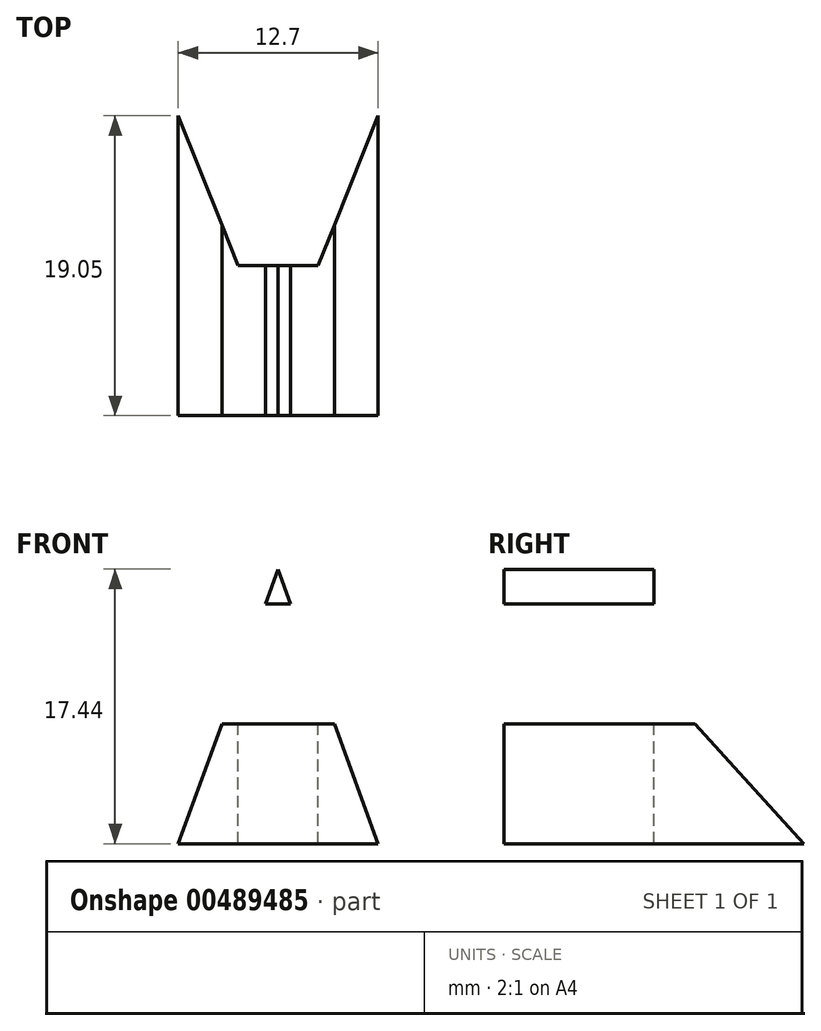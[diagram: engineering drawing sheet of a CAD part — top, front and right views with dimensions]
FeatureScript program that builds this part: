
annotation { "Feature Type Name" : "Feature", "Feature Type Description" : "" }
export const myFeature = defineFeature(function(context is Context, id is Id, definition is map)
    precondition{}
    {
        {
            var Q0;
            Q0=qCreatedBy(makeId("Front.planeOp"),FACE);
            var sketch = newSketch(context, id + "F0", { "sketchPlane" : qUnion([Q0])});
            skLineSegment(sketch, "E0", {"start": v(0, 0) * mm, "end": v(38.1, 0) * mm});
            skLineSegment(sketch, "E1", {"start": v(38.1, 0) * mm, "end": v(38.1, 38.1) * mm});
            skLineSegment(sketch, "E2", {"start": v(38.1, 38.1) * mm, "end": v(0, 38.1) * mm});
            skLineSegment(sketch, "E3", {"start": v(0, 38.1) * mm, "end": v(0, 0) * mm});
            skSolve(sketch);
        }
        {
            var Q0;
            Q0=makeQuery(id+"F0.imprint","IMPRINT",FACE,{"disambiguationData":[TD([[makeQuery(id+"F0.imprint","IMPRINT",EDGE,{"derivedFrom":sQuery(id+"F0.wireOp",EDGE,"E0")}),1.0]])]});
            extrude(context, id + "F1", {"entities" : qUnion([Q0]), "depth" : 38.1 * mm, "offsetDistance" : 25.4 * mm});
        }
        {
            var Q0;
            Q0=qCreatedBy(makeId("Front.planeOp"),FACE);
            cPlane(context, id + "F2", {"entities" : qUnion([Q0]), "cplaneType" : CPlaneType.OFFSET, "offset" : 38.1 * mm, "width" : 152.4 * mm, "height" : 152.4 * mm});
        }
        {
            var Q0;
            Q0=qCreatedBy(makeId("Right.planeOp"),FACE);
            cPlane(context, id + "F3", {"entities" : qUnion([Q0]), "cplaneType" : CPlaneType.OFFSET, "offset" : 38.1 * mm, "width" : 152.4 * mm, "height" : 152.4 * mm});
        }
        {
            var Q0;
            Q0=qCreatedBy(makeId("Top.planeOp"),FACE);
            cPlane(context, id + "F4", {"entities" : qUnion([Q0]), "cplaneType" : CPlaneType.OFFSET, "offset" : 38.1 * mm, "width" : 152.4 * mm, "height" : 152.4 * mm});
        }
        {
            var Q0;
            Q0=qCreatedBy(id+"F3.planeOp",FACE);
            var sketch = newSketch(context, id + "F5", { "sketchPlane" : qUnion([Q0])});
            skLineSegment(sketch, "E4", {"start": v(0, 0) * mm, "end": v(0, 38.1) * mm});
            skLineSegment(sketch, "E5", {"start": v(0, 38.1) * mm, "end": v(-38.1, 38.1) * mm});
            skLineSegment(sketch, "E6", {"start": v(-38.1, 38.1) * mm, "end": v(-38.1, 0) * mm});
            skLineSegment(sketch, "E7", {"start": v(-38.1, 0) * mm, "end": v(0, 0) * mm});
            skLineSegment(sketch, "E8", {"start": v(0, 30.48) * mm, "end": v(-25.4, 30.48) * mm});
            skLineSegment(sketch, "E9", {"start": v(-25.4, 30.48) * mm, "end": v(-25.4, 22.86) * mm});
            skLineSegment(sketch, "E10", {"start": v(-25.4, 22.86) * mm, "end": v(0, 22.86) * mm});
            skLineSegment(sketch, "E11", {"start": v(-38.1, 15.24) * mm, "end": v(-12.7, 15.24) * mm});
            skLineSegment(sketch, "E12", {"start": v(-12.7, 15.24) * mm, "end": v(-12.7, 7.62) * mm});
            skLineSegment(sketch, "E13", {"start": v(-12.7, 7.62) * mm, "end": v(-38.1, 7.62) * mm});
            skSolve(sketch);
        }
        {
            var Q0;
            {var subQ0=sQuery(id+"F5.wireOp",EDGE,"E8");Q0=makeQuery(id+"F5.imprint","IMPRINT",FACE,{"disambiguationData":[TD([[makeQuery(id+"F5.imprint","IMPRINT",EDGE,{"derivedFrom":subQ0}),1.0]])]});}
            var Q1;
            {var subQ0=sQuery(id+"F5.wireOp",EDGE,"E11");Q1=makeQuery(id+"F5.imprint","IMPRINT",FACE,{"disambiguationData":[TD([[makeQuery(id+"F5.imprint","IMPRINT",EDGE,{"derivedFrom":subQ0}),-1.0]])]});}
            extrude(context, id + "F6", {"entities" : qUnion([Q0, Q1]), "operationType" : NewBodyOperationType.REMOVE, "oppositeDirection" : true, "depth" : 38.1 * mm, "offsetDistance" : 25.4 * mm});
        }
        {
            var Q0;
            Q0=qCreatedBy(id+"F2.planeOp",FACE);
            var sketch = newSketch(context, id + "F7", { "sketchPlane" : qUnion([Q0])});
            skLineSegment(sketch, "E14", {"start": v(0, 0) * mm, "end": v(38.1, 0) * mm});
            skLineSegment(sketch, "E15", {"start": v(38.1, 0) * mm, "end": v(38.1, 38.1) * mm});
            skLineSegment(sketch, "E16", {"start": v(38.1, 38.1) * mm, "end": v(0, 38.1) * mm});
            skLineSegment(sketch, "E17", {"start": v(0, 38.1) * mm, "end": v(0, 0) * mm});
            skLineSegment(sketch, "E18", {"start": v(12.7, 38.1) * mm, "end": v(25.4, 38.1) * mm});
            skLineSegment(sketch, "E19", {"start": v(25.4, 38.1) * mm, "end": v(38.1, 0) * mm});
            skLineSegment(sketch, "E20", {"start": v(12.7, 38.1) * mm, "end": v(0, 0) * mm});
            skLineSegment(sketch, "E21", {"start": v(0, 0) * mm, "end": v(12.7, 0) * mm});
            skLineSegment(sketch, "E22", {"start": v(12.7, 0) * mm, "end": v(19.05, 17.44) * mm});
            skLineSegment(sketch, "E23", {"start": v(38.1, 0) * mm, "end": v(25.4, 0) * mm});
            skLineSegment(sketch, "E24", {"start": v(25.4, 0) * mm, "end": v(19.05, 17.44) * mm});
            skLineSegment(sketch, "E25", {"start": v(19.5, 35.03) * mm, "end": v(15.48, 22.98) * mm});
            skLineSegment(sketch, "E26", {"start": v(15.48, 22.98) * mm, "end": v(23.52, 22.98) * mm});
            skLineSegment(sketch, "E27", {"start": v(19.5, 35.03) * mm, "end": v(23.52, 22.98) * mm});
            skSolve(sketch);
        }
        {
            var Q0;
            {var subQ0=sQuery(id+"F7.wireOp",EDGE,"E17");Q0=makeQuery(id+"F7.imprint","IMPRINT",FACE,{"disambiguationData":[TD([[makeQuery(id+"F7.imprint","IMPRINT",EDGE,{"derivedFrom":subQ0}),1.0]])]});}
            var Q1;
            Q1=makeQuery(id+"F7.imprint","IMPRINT",FACE,{"disambiguationData":[TD([[makeQuery(id+"F7.imprint","IMPRINT",EDGE,{"derivedFrom":sQuery(id+"F7.wireOp",EDGE,"E14")}),1.0]])]});
            var Q2;
            Q2=makeQuery(id+"F7.imprint","IMPRINT",FACE,{"disambiguationData":[TD([[makeQuery(id+"F7.imprint","IMPRINT",EDGE,{"derivedFrom":sQuery(id+"F7.wireOp",EDGE,"E25")}),1.0]])]});
            var Q3;
            {var subQ0=sQuery(id+"F7.wireOp",EDGE,"E15");Q3=makeQuery(id+"F7.imprint","IMPRINT",FACE,{"disambiguationData":[TD([[makeQuery(id+"F7.imprint","IMPRINT",EDGE,{"derivedFrom":subQ0}),1.0]])]});}
            extrude(context, id + "F8", {"entities" : qUnion([Q0, Q1, Q2, Q3]), "operationType" : NewBodyOperationType.REMOVE, "oppositeDirection" : true, "depth" : 38.1 * mm, "offsetDistance" : 25.4 * mm});
        }
        {
            var Q0;
            Q0=qCreatedBy(id+"F4.planeOp",FACE);
            var sketch = newSketch(context, id + "F9", { "sketchPlane" : qUnion([Q0])});
            skLineSegment(sketch, "E28", {"start": v(0, 0) * mm, "end": v(38.1, 0) * mm});
            skLineSegment(sketch, "E29", {"start": v(38.1, 0) * mm, "end": v(38.1, -38.1) * mm});
            skLineSegment(sketch, "E30", {"start": v(38.1, -38.1) * mm, "end": v(0, -38.1) * mm});
            skLineSegment(sketch, "E31", {"start": v(0, -38.1) * mm, "end": v(0, 0) * mm});
            skPoint(sketch, "E32.endSnap0", {"position": v(19.05, 0) * mm});
            skLineSegment(sketch, "E33", {"start": v(6.35, 0) * mm, "end": v(12.7, 0) * mm});
            skLineSegment(sketch, "E34", {"start": v(6.35, 0) * mm, "end": v(0, -38.1) * mm});
            skLineSegment(sketch, "E35", {"start": v(12.7, 0) * mm, "end": v(19.05, -15.87) * mm});
            skLineSegment(sketch, "E36", {"start": v(19.05, -15.88) * mm, "end": v(25.4, 0) * mm});
            skLineSegment(sketch, "E37", {"start": v(25.4, 0) * mm, "end": v(31.75, 0) * mm});
            skLineSegment(sketch, "E38", {"start": v(31.75, 0) * mm, "end": v(38.1, -38.1) * mm});
            skLineSegment(sketch, "E39", {"start": v(38.1, -38.1) * mm, "end": v(31.75, -38.1) * mm});
            skLineSegment(sketch, "E40", {"start": v(31.75, -38.1) * mm, "end": v(26.67, -15.88) * mm});
            skLineSegment(sketch, "E41", {"start": v(26.67, -15.88) * mm, "end": v(21.6, -28.58) * mm});
            skLineSegment(sketch, "E42", {"start": v(0, -38.1) * mm, "end": v(6.35, -38.1) * mm});
            skLineSegment(sketch, "E43", {"start": v(6.35, -38.1) * mm, "end": v(11.43, -15.88) * mm});
            skLineSegment(sketch, "E44", {"start": v(11.43, -15.88) * mm, "end": v(16.51, -28.58) * mm});
            skLineSegment(sketch, "E45", {"start": v(16.51, -28.58) * mm, "end": v(21.6, -28.58) * mm});
            skSolve(sketch);
        }
        {
            var Q0;
            {var subQ0=sQuery(id+"F9.wireOp",EDGE,"E31");Q0=makeQuery(id+"F9.imprint","IMPRINT",FACE,{"disambiguationData":[TD([[makeQuery(id+"F9.imprint","IMPRINT",EDGE,{"derivedFrom":subQ0}),-1.0]])]});}
            var Q1;
            Q1=makeQuery(id+"F9.imprint","IMPRINT",FACE,{"disambiguationData":[TD([[makeQuery(id+"F9.imprint","IMPRINT",EDGE,{"derivedFrom":sQuery(id+"F9.wireOp",EDGE,"E30")}),-1.0]])]});
            var Q2;
            {var subQ0=sQuery(id+"F9.wireOp",EDGE,"E35");Q2=makeQuery(id+"F9.imprint","IMPRINT",FACE,{"disambiguationData":[TD([[makeQuery(id+"F9.imprint","IMPRINT",EDGE,{"derivedFrom":subQ0}),1.0]])]});}
            var Q3;
            {var subQ0=sQuery(id+"F9.wireOp",EDGE,"E29");Q3=makeQuery(id+"F9.imprint","IMPRINT",FACE,{"disambiguationData":[TD([[makeQuery(id+"F9.imprint","IMPRINT",EDGE,{"derivedFrom":subQ0}),-1.0]])]});}
            extrude(context, id + "F10", {"entities" : qUnion([Q0, Q1, Q2, Q3]), "operationType" : NewBodyOperationType.REMOVE, "oppositeDirection" : true, "depth" : 38.1 * mm, "offsetDistance" : 25.4 * mm});
        }
    });
